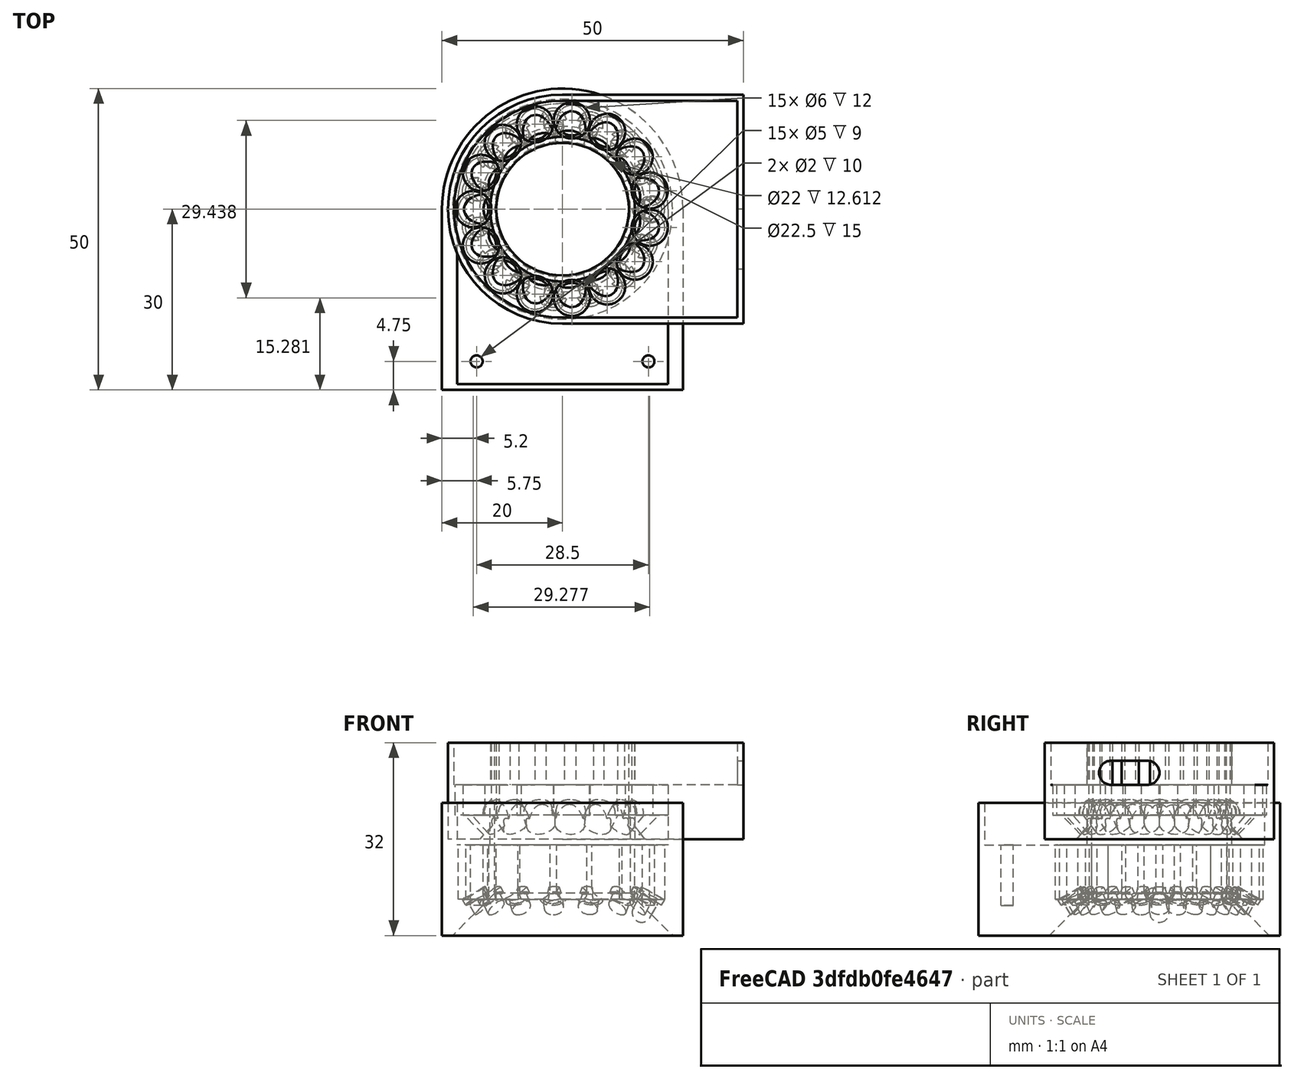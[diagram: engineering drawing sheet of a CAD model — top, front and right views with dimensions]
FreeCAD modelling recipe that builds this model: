
FCSTD DOCUMENT  (FreeCAD 0.21R33771 (Git))
Label: microscope-lamp-body
License: All rights reserved
LicenseURL: http://en.wikipedia.org/wiki/All_rights_reserved
objects: Sketcher::SketchObject×8, PartDesign::Pocket×6, Part::Cut×4, Part::Cylinder×4, PartDesign::Body×3, Part::FeaturePython×2, Part::Refine×2, Mesh::Feature×2, Part::MultiFuse×2, PartDesign::Pad×1, PartDesign::Chamfer×1, PartDesign::PolarPattern×1, PartDesign::Revolution×1, Part::Box×1, Part::Cone×1, PartDesign::FeatureBase×1
note: 46 computed .brp shape members not serialized (recipe doc carries the construction recipe); baked Part::Feature solids carry a one-line shape summary decoded from their .brp

FEATURE [Sketcher::SketchObject] Sketch
  FullyConstrained = true
  MapMode = 5
  Support = -> [XY_Plane]
  sketch-geometry (7):
    g0: Circle CenterX=0 CenterY=0 CenterZ=0 NormalX=0 NormalY=0 NormalZ=1 AngleXU=0 Radius=11.25
    g1: ArcOfCircle CenterX=0 CenterY=0 CenterZ=0 NormalX=0 NormalY=0 NormalZ=1 AngleXU=0 Radius=20 StartAngle=0 EndAngle=3.14159
    g2: LineSegment StartX=-20 StartY=4.732e-13 StartZ=0 EndX=20 EndY=0 EndZ=0
    g3: LineSegment StartX=20 StartY=0 StartZ=0 EndX=20 EndY=-30 EndZ=0
    g4: LineSegment StartX=20 StartY=-30 StartZ=0 EndX=-20 EndY=-30 EndZ=0
    g5: LineSegment StartX=-20 StartY=-30 StartZ=0 EndX=-20 EndY=4.725e-13 EndZ=0
    g6: GeomPoint X=0 Y=20 Z=0
  constraints (18):
    c: Coincident(g0,g-1)
    c: Coincident(g1,g0)
    c: PointOnObject(g1,g-1)
    c: PointOnObject(g1,g-1)
    c: Coincident(g2,g3)
    c: Coincident(g3,g4)
    c: Coincident(g4,g5)
    c: Coincident(g5,g2)
    c: Horizontal(g4)
    c: Vertical(g3)
    c: Vertical(g5)
    c: Coincident(g2,g1)
    c: Coincident(g2,g1)
    c: Diameter(g0) = 22.5
    c: PointOnObject(g6,g-2)
    c: PointOnObject(g6,g1)
    c: DistanceY(g5,g5) = 30
    c: DistanceX(g2,g2) = 40
FEATURE [PartDesign::Pad] Pad
  Direction = (0,0,1)
  Length = 22
  Length2 = 10
  Profile = -> Sketch
  ReferenceAxis = -> Sketch [N_Axis]
  Reversed = true
  Type = 0
FEATURE [PartDesign::Chamfer] Chamfer
  Angle = 45
  Base = -> Pad [Edge15]
  BaseFeature = -> Pad
  ChamferType = 1
  FlipDirection = false
  Size = 7
  Size2 = 7
  SupportTransform = false
  UseAllEdges = false
FEATURE [Sketcher::SketchObject] Sketch001
  FullyConstrained = true
  MapMode = 5
  Support = -> [Chamfer]
  sketch-geometry (6):
    g0: ArcOfCircle CenterX=0 CenterY=0 CenterZ=0 NormalX=0 NormalY=0 NormalZ=1 AngleXU=0 Radius=17.5 StartAngle=0 EndAngle=3.14159
    g1: LineSegment StartX=-17.5 StartY=1.517e-12 StartZ=0 EndX=17.5 EndY=0 EndZ=0
    g2: LineSegment StartX=17.5 StartY=0 StartZ=0 EndX=17.5 EndY=-29 EndZ=0
    g3: LineSegment StartX=17.5 StartY=-29 StartZ=0 EndX=-17.5 EndY=-29 EndZ=0
    g4: LineSegment StartX=-17.5 StartY=-29 StartZ=0 EndX=-17.5 EndY=1.517e-12 EndZ=0
    g5: Circle CenterX=0 CenterY=0 CenterZ=0 NormalX=0 NormalY=0 NormalZ=1 AngleXU=0 Radius=12
  constraints (16):
    c: Coincident(g0,g-1)
    c: PointOnObject(g0,g-1)
    c: PointOnObject(g0,g-1)
    c: Coincident(g1,g2)
    c: Coincident(g2,g3)
    c: Coincident(g3,g4)
    c: Coincident(g4,g1)
    c: Horizontal(g3)
    c: Vertical(g2)
    c: Vertical(g4)
    c: Coincident(g1,g0)
    c: Coincident(g1,g0)
    c: Coincident(g5,g0)
    c: Diameter(g5) = 24
    c: DistanceX(g1,g1) = 35
    c: DistanceY(g3,g0) = 29
FEATURE [PartDesign::Pocket] Pocket
  BaseFeature = -> Chamfer
  Direction = (0,0,-1)
  Length = 7
  Length2 = 5
  Profile = -> Sketch001
  ReferenceAxis = -> Sketch001 [N_Axis]
  Type = 0
FEATURE [Sketcher::SketchObject] Sketch002
  FullyConstrained = true
  MapMode = 5
  Placement = pos=(0,0,-7) rot=(0,0,1;0rad)
  Support = -> [Pocket]
  sketch-geometry (2):
    g0: Circle CenterX=14.25 CenterY=-25.2505 CenterZ=0 NormalX=0 NormalY=0 NormalZ=1 AngleXU=0 Radius=1
    g1: Circle CenterX=-14.25 CenterY=-25.2505 CenterZ=0 NormalX=0 NormalY=0 NormalZ=1 AngleXU=0 Radius=1
  constraints (5):
    c: Symmetric(g1,g0,g-2)
    c: Equal(g0,g1)
    c: Diameter(g0) = 2
    c: DistanceX(g1,g0) = 28.5
    c: Distance(g-1,g0) = 28.994
FEATURE [PartDesign::Pocket] Pocket001
  BaseFeature = -> Pocket
  Direction = (0,0,-1)
  Length = 10
  Length2 = 5
  Profile = -> Sketch002
  ReferenceAxis = -> Sketch002 [N_Axis]
  Type = 0
FEATURE [Sketcher::SketchObject] Sketch003
  FullyConstrained = true
  MapMode = 5
  Placement = pos=(0,0,-7) rot=(0,0,1;0rad)
  Support = -> [Pocket001]
  sketch-geometry (1):
    g0: Circle CenterX=-14.8 CenterY=0 CenterZ=0 NormalX=0 NormalY=0 NormalZ=1 AngleXU=0 Radius=2.5
  constraints (3):
    c: PointOnObject(g0,g-1)
    c: Diameter(g0) = 5
    c: DistanceX(g0,g-1) = 14.8
FEATURE [PartDesign::Pocket] Pocket002
  BaseFeature = -> Pocket001
  Direction = (0,0,-1)
  Length = 9
  Length2 = 5
  Profile = -> Sketch003
  ReferenceAxis = -> Sketch003 [N_Axis]
  Type = 0
FEATURE [PartDesign::PolarPattern] PolarPattern
  Angle = 360
  Axis = -> Sketch003 [N_Axis]
  BaseFeature = -> Pocket002
  Occurrences = 15
  Originals = -> [Pocket002]
FEATURE [PartDesign::Body] Body  label="Zawartość"
  Group = -> [Sketch,Pad,Chamfer,Sketch001,Pocket,Sketch002,Pocket001,Sketch003,Pocket002,PolarPattern]
  Origin = -> Origin
  Tip = -> PolarPattern
FEATURE [Sketcher::SketchObject] Sketch004
  FullyConstrained = true
  MapMode = 5
  Placement = pos=(0,0,0) rot=(1,0,0;1.5708rad)
  Support = -> [XZ_Plane001]
  sketch-geometry (7):
    g0: ArcOfCircle CenterX=0 CenterY=-3.7 CenterZ=0 NormalX=0 NormalY=0 NormalZ=1 AngleXU=0 Radius=1.6 StartAngle=4.71239 EndAngle=6.28319
    g1: LineSegment StartX=1.6 StartY=-3.7 StartZ=0 EndX=0 EndY=-3.7 EndZ=0
    g2: LineSegment StartX=1.6 StartY=-3.7 StartZ=0 EndX=1.6 EndY=-1 EndZ=0
    g3: LineSegment StartX=1.6 StartY=-1 StartZ=0 EndX=2.2 EndY=-1 EndZ=0
    g4: LineSegment StartX=2.2 StartY=-1 StartZ=0 EndX=2.2 EndY=0 EndZ=0
    g5: LineSegment StartX=2.2 StartY=0 StartZ=0 EndX=0 EndY=0 EndZ=0
    g6: LineSegment StartX=0 StartY=0 StartZ=0 EndX=-3e-16 EndY=-5.3 EndZ=0
  constraints (20):
    c: PointOnObject(g0,g-2)
    c: PointOnObject(g0,g-2)
    c: Coincident(g1,g0)
    c: Coincident(g1,g0)
    c: Horizontal(g1)
    c: Coincident(g2,g0)
    c: Vertical(g2)
    c: Coincident(g3,g2)
    c: Coincident(g4,g3)
    c: Vertical(g4)
    c: Coincident(g5,g4)
    c: Horizontal(g5)
    c: Coincident(g6,g5)
    c: Coincident(g6,g0)
    c: Horizontal(g3)
    c: DistanceX(g1,g1) = 1.6
    c: DistanceY(g4,g4) = 1
    c: DistanceY(g0,g4) = 5.3
    c: DistanceX(g5,g5) = 2.2
    c: Coincident(g5,g-1)
FEATURE [PartDesign::Revolution] Revolution
  Angle = 360
  Axis = (0,-2e-16,1)
  Base = (0,0,0)
  Placement = pos=(0,0,0) rot=(1,0,0;1.5708rad)
  Profile = -> Sketch004
  ReferenceAxis = -> Sketch004 [V_Axis]
  Reversed = true
FEATURE [PartDesign::Body] Body001  label="LED"
  Group = -> [Sketch004,Revolution]
  Origin = -> Origin001
  Placement = pos=(15,0,-15) rot=(0,1,0;0.523599rad)
  Tip = -> Revolution
FEATURE [Part::FeaturePython] Array  # Draft array (typed FeaturePython)
  AlwaysSyncPlacement = false
  Angle = 360
  ArrayType = 1
  Axis = (0,0,1)
  Base = -> Body001
  Center = (0,0,0)
  Count = 15
  ExpandArray = false
  Fuse = false
  IntervalAxis = (0,0,0)
  IntervalX = (50,0,0)
  IntervalY = (0,50,0)
  IntervalZ = (0,0,50)
  NumberCircles = 3
  NumberPolar = 15
  NumberX = 2
  NumberY = 2
  NumberZ = 1
  PlacementList = 15 placements: [(15,0,-15),(13.7032,6.10105,-15),(10.037,11.1472,-15),(4.63525,14.2658,-15),(-1.56793,14.9178,-15),(-7.5,12.9904,-15),(-12.1353,8.81678,-15),(-14.6722,3.11868,-15),(-14.6722,-3.11868,-15),(-12.1353,-8.81678,-15),(-7.5,-12.9904,-15),(-1.56793,-14.9178,-15),(4.63525,-14.2658,-15),(10.037,-11.1472,-15),(13.7032,-6.10105,-15)]
  RadialDistance = 50
  ScaleList = (15) [(1,1,1),(1,1,1),(1,1,1),(1,1,1),(1,1,1),(1,1,1),(1,1,1),(1,1,1),(1,1,1),(1,1,1),(1,1,1),(1,1,1),(1,1,1),(1,1,1),(1,1,1)]
  Symmetry = 1
  TangentialDistance = 25
FEATURE [Part::Cut] Cut
  Base = -> Body
  Tool = -> Array
FEATURE [Part::Refine] Cut001
  Source = -> Cut
FEATURE [Mesh::Feature] Mesh  label="Zawartość001 (Meshed)"
FEATURE [Part::Cylinder] Cylinder  label="Walec"
  Angle = 360
  AttacherType = Attacher::AttachEngine3D
  FirstAngle = 0
  Height = 10
  Placement = pos=(0,0,0) rot=(0,1,0;-2.35619rad)
  Radius = 2.5
  SecondAngle = 0
FEATURE [Part::Cylinder] Cylinder001  label="Walec001"
  Angle = 360
  AttacherType = Attacher::AttachEngine3D
  FirstAngle = 0
  Height = 25
  Placement = pos=(0,0,-2) rot=(0,0,1;0rad)
  Radius = 3
  SecondAngle = 0
FEATURE [Part::MultiFuse] Fusion
  Placement = pos=(-14.8,0,0) rot=(0,0,1;3.14159rad)
  Shapes = -> [Cylinder,Cylinder001]
FEATURE [Part::FeaturePython] Array001  # Draft array (typed FeaturePython)
  AlwaysSyncPlacement = false
  Angle = 360
  ArrayType = 1
  Axis = (0,0,1)
  Base = -> Fusion
  Center = (0,0,0)
  Count = 15
  ExpandArray = false
  Fuse = true
  IntervalAxis = (0,0,0)
  IntervalX = (50,0,0)
  IntervalY = (0,50,0)
  IntervalZ = (0,0,50)
  NumberCircles = 3
  NumberPolar = 15
  NumberX = 2
  NumberY = 2
  NumberZ = 1
  PlacementList = 15 placements: [(-14.8,0,0),(-13.5205,-6.0197,0),(-9.90313,-10.9985,0),(-4.57345,-14.0756,0),(1.54702,-14.7189,0),(7.4,-12.8172,0),(11.9735,-8.69922,0),(14.4766,-3.07709,0),(14.4766,3.07709,0),(11.9735,8.69922,0),(7.4,12.8172,0),(1.54702,14.7189,0),(-4.57345,14.0756,0),(-9.90313,10.9985,0),(-13.5205,6.0197,0)]
  RadialDistance = 50
  ScaleList = (15) [(1,1,1),(1,1,1),(1,1,1),(1,1,1),(1,1,1),(1,1,1),(1,1,1),(1,1,1),(1,1,1),(1,1,1),(1,1,1),(1,1,1),(1,1,1),(1,1,1),(1,1,1)]
  Symmetry = 1
  TangentialDistance = 25
FEATURE [Part::Cylinder] Cylinder002  label="Walec002"
  Angle = 360
  AttacherType = Attacher::AttachEngine3D
  FirstAngle = 0
  Height = 100
  Placement = pos=(0,0,-50) rot=(0,0,1;0rad)
  Radius = 11
  SecondAngle = 0
FEATURE [Part::Cylinder] Cylinder003  label="Walec003"
  Angle = 360
  AttacherType = Attacher::AttachEngine3D
  FirstAngle = 0
  Height = 20
  Placement = pos=(0,0,-10) rot=(0,0,1;0rad)
  Radius = 19
  SecondAngle = 0
FEATURE [Part::Box] Box  label="Sześcian"
  AttacherType = Attacher::AttachEngine3D
  Height = 20
  Length = 30
  Placement = pos=(0,-19,-10) rot=(0,0,1;0rad)
  Width = 38
FEATURE [Part::MultiFuse] Fusion001
  Shapes = -> [Cylinder003,Box]
FEATURE [Part::Cut] Cut002
  Base = -> Fusion001
  Tool = -> Cylinder002
FEATURE [Part::Cut] Cut003
  Base = -> Cut002
  Tool = -> Array001
FEATURE [Part::Cone] Cone  label="Stożek"
  Angle = 360
  AttacherType = Attacher::AttachEngine3D
  Height = 11
  Placement = pos=(0,0,-10) rot=(0,0,1;0rad)
  Radius1 = 17
  Radius2 = 8
FEATURE [Part::Cut] Cut004
  Base = -> Cut003
  Tool = -> Cone
FEATURE [Part::Refine] Cut005
  Source = -> Cut004
FEATURE [PartDesign::FeatureBase] BaseFeature
  BaseFeature = -> Cut005
FEATURE [Sketcher::SketchObject] Sketch006
  FullyConstrained = true
  MapMode = 5
  Placement = pos=(0,0,10) rot=(0,0,1;0rad)
  Support = -> [BaseFeature]
  sketch-geometry (5):
    g0: ArcOfCircle CenterX=0 CenterY=0 CenterZ=0 NormalX=0 NormalY=0 NormalZ=1 AngleXU=0 Radius=18 StartAngle=1.5708 EndAngle=4.71239
    g1: LineSegment StartX=1.1e-15 StartY=18 StartZ=0 EndX=29 EndY=18 EndZ=0
    g2: LineSegment StartX=29 StartY=18 StartZ=0 EndX=29 EndY=-18 EndZ=0
    g3: LineSegment StartX=29 StartY=-18 StartZ=0 EndX=-3.6e-15 EndY=-18 EndZ=0
    g4: Circle CenterX=0 CenterY=0 CenterZ=0 NormalX=0 NormalY=0 NormalZ=1 AngleXU=0 Radius=12
  constraints (14):
    c: Coincident(g0,g-1)
    c: PointOnObject(g0,g-2)
    c: PointOnObject(g0,g-2)
    c: Coincident(g1,g0)
    c: Horizontal(g1)
    c: Coincident(g2,g1)
    c: Vertical(g2)
    c: Coincident(g3,g2)
    c: Coincident(g3,g0)
    c: Horizontal(g3)
    c: DistanceY(g2,g2) = 36
    c: DistanceX(g3,g3) = 29
    c: Coincident(g4,g0)
    c: Diameter(g4) = 24
FEATURE [PartDesign::Pocket] Pocket003
  BaseFeature = -> BaseFeature
  Direction = (0,0,-1)
  Length = 7
  Length2 = 5
  Profile = -> Sketch006
  ReferenceAxis = -> Sketch006 [N_Axis]
  Type = 0
FEATURE [Sketcher::SketchObject] Sketch007
  ExternalGeometry = -> [Pocket003]
  FullyConstrained = true
  MapMode = 5
  Placement = pos=(29,0,0) rot=(0.57735,-0.57735,-0.57735;2.0944rad)
  Support = -> [Pocket003]
  sketch-geometry (7):
    g0: ArcOfCircle CenterX=2 CenterY=5 CenterZ=0 NormalX=0 NormalY=0 NormalZ=1 AngleXU=0 Radius=2 StartAngle=1.5708 EndAngle=4.71239
    g1: ArcOfCircle CenterX=8 CenterY=5 CenterZ=0 NormalX=0 NormalY=0 NormalZ=1 AngleXU=0 Radius=2 StartAngle=4.71239 EndAngle=7.85398
    g2: LineSegment StartX=2 StartY=3 StartZ=0 EndX=8 EndY=3 EndZ=0
    g3: LineSegment StartX=8 StartY=7 StartZ=0 EndX=2 EndY=7 EndZ=0
    g4: LineSegment StartX=1.09e-14 StartY=5 StartZ=0 EndX=10 EndY=5 EndZ=0
    g5: LineSegment StartX=2 StartY=3 StartZ=0 EndX=8 EndY=7 EndZ=0
    g6: GeomPoint X=5 Y=5 Z=0
  constraints (18):
    c: Tangent(g0,g2) = -1.5708
    c: Tangent(g2,g1) = -1.5708
    c: Tangent(g1,g3) = -1.5708
    c: Tangent(g3,g0) = -1.5708
    c: Equal(g0,g1)
    c: Horizontal(g2)
    c: PointOnObject(g4,g0)
    c: PointOnObject(g4,g1)
    c: Horizontal(g4)
    c: PointOnObject(g1,g4)
    c: DistanceX(g4,g4) = 10
    c: DistanceY(g1,g1) = 4
    c: PointOnObject(g0,g-3)
    c: Coincident(g5,g0)
    c: Coincident(g5,g1)
    c: PointOnObject(g6,g5)
    c: PointOnObject(g6,g4)
    c: DistanceX(g-1,g6) = 5
FEATURE [PartDesign::Pocket] Pocket004
  BaseFeature = -> Pocket003
  Direction = (1,0,0)
  Length = 5
  Length2 = 5
  Profile = -> Sketch007
  ReferenceAxis = -> Sketch007 [N_Axis]
  Type = 1
FEATURE [Sketcher::SketchObject] Sketch008
  ExternalGeometry = -> [Pocket004]
  FullyConstrained = true
  MapMode = 5
  Placement = pos=(0,0,-10) rot=(1,0,0;3.14159rad)
  Support = -> [Pocket004]
  sketch-geometry (4):
    g0: ArcOfCircle CenterX=0 CenterY=0 CenterZ=0 NormalX=0 NormalY=0 NormalZ=1 AngleXU=0 Radius=19 StartAngle=1.5708 EndAngle=4.71239
    g1: LineSegment StartX=0 StartY=19 StartZ=0 EndX=30 EndY=19 EndZ=0
    g2: LineSegment StartX=30 StartY=19 StartZ=0 EndX=30 EndY=-19 EndZ=0
    g3: LineSegment StartX=30 StartY=-19 StartZ=0 EndX=0 EndY=-19 EndZ=0
  constraints (9):
    c: Coincident(g0,g-1)
    c: Coincident(g0,g-3)
    c: Coincident(g1,g0)
    c: Coincident(g1,g-3)
    c: Coincident(g2,g1)
    c: Coincident(g2,g-4)
    c: Coincident(g3,g2)
    c: Coincident(g3,g0)
    c: PointOnObject(g0,g-2)
FEATURE [PartDesign::Pocket] Pocket005
  BaseFeature = -> Pocket004
  Direction = (0,0,1)
  Length = 4
  Length2 = 5
  Profile = -> Sketch008
  ReferenceAxis = -> Sketch008 [N_Axis]
  Type = 0
FEATURE [PartDesign::Body] Body003
  BaseFeature = -> Cut005
  Group = -> [BaseFeature,Sketch006,Pocket003,Sketch007,Pocket004,Sketch008,Pocket005]
  Origin = -> Origin003
  Tip = -> Pocket005
FEATURE [Mesh::Feature] Mesh001  label="Pocket005 (Meshed)"
